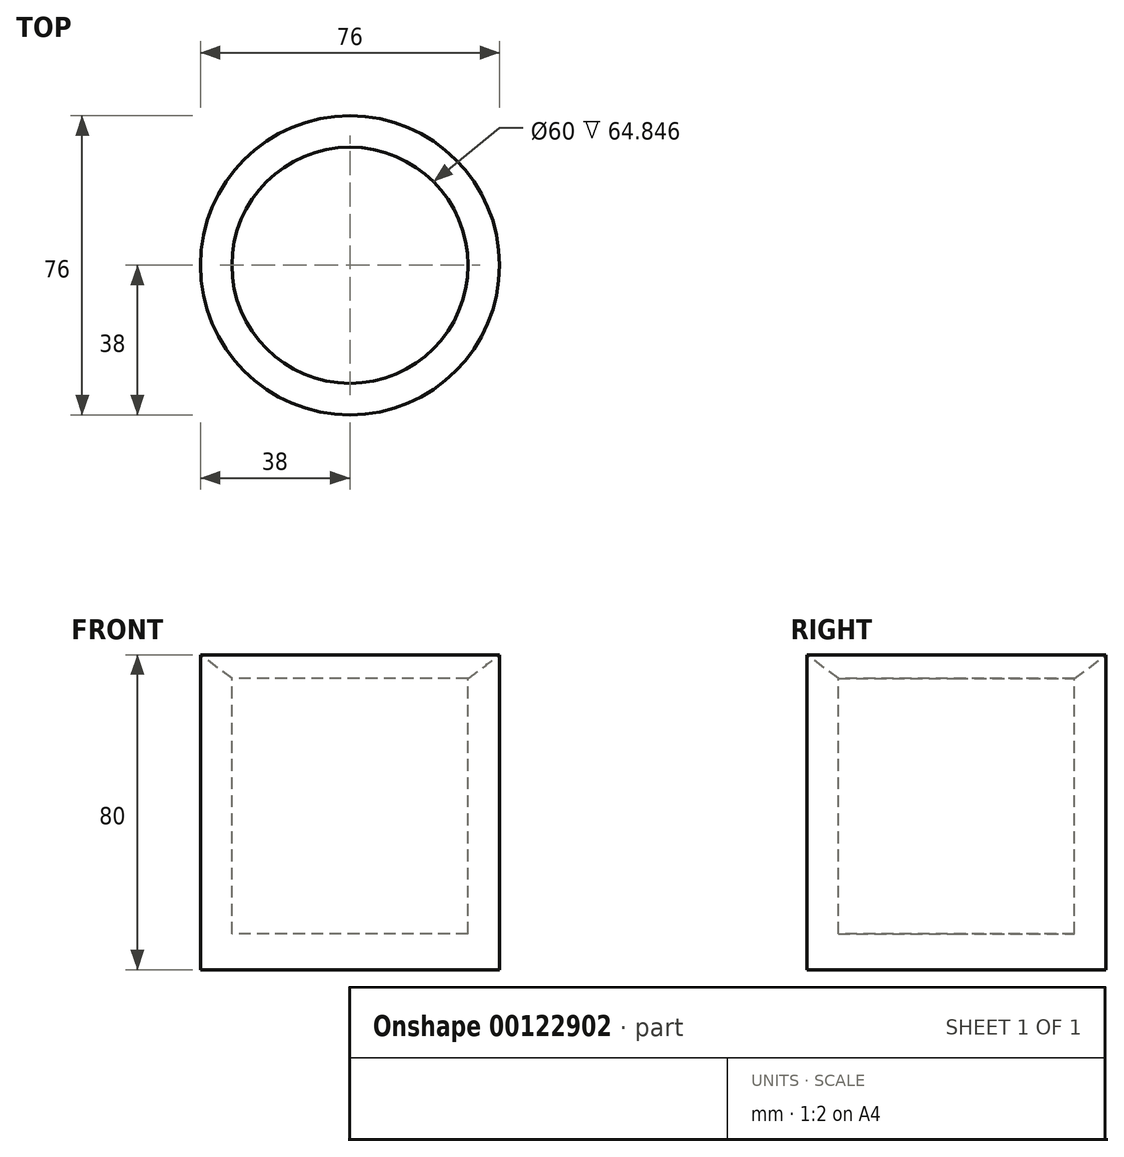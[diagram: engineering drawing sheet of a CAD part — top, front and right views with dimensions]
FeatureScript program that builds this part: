
annotation { "Feature Type Name" : "Feature", "Feature Type Description" : "" }
export const myFeature = defineFeature(function(context is Context, id is Id, definition is map)
    precondition{}
    {
        {
            var Q0;
            Q0=qCreatedBy(makeId("Front.planeOp"),FACE);
            var sketch = newSketch(context, id + "F0", { "sketchPlane" : qUnion([Q0])});
            skLineSegment(sketch, "E0", {"start": v(0, 0) * mm, "end": v(-38, 0) * mm});
            skLineSegment(sketch, "E1", {"start": v(-38, 0) * mm, "end": v(-38, 80) * mm});
            skLineSegment(sketch, "E2", {"start": v(-38, 80) * mm, "end": v(-30, 73.98) * mm});
            skLineSegment(sketch, "E3", {"start": v(-30, 73.98) * mm, "end": v(-30, 9.14) * mm});
            skLineSegment(sketch, "E4", {"start": v(-30, 9.14) * mm, "end": v(0, 9.14) * mm});
            skLineSegment(sketch, "E5", {"start": v(0, 9.14) * mm, "end": v(0, 0) * mm});
            skSolve(sketch);
        }
        {
            var Q0;
            Q0=makeQuery(id+"F0.imprint","IMPRINT",FACE,{"disambiguationData":[TD([[makeQuery(id+"F0.imprint","IMPRINT",EDGE,{"derivedFrom":sQuery(id+"F0.wireOp",EDGE,"E0")}),-1.0]])]});
            var Q1;
            Q1=sQuery(id+"F0.wireOp",EDGE,"E5");
            revolve(context, id + "F1", {"entities" : qUnion([Q0]), "axis" : qUnion([Q1]), "revolveType" : RevolveType.FULL});
        }
    });
